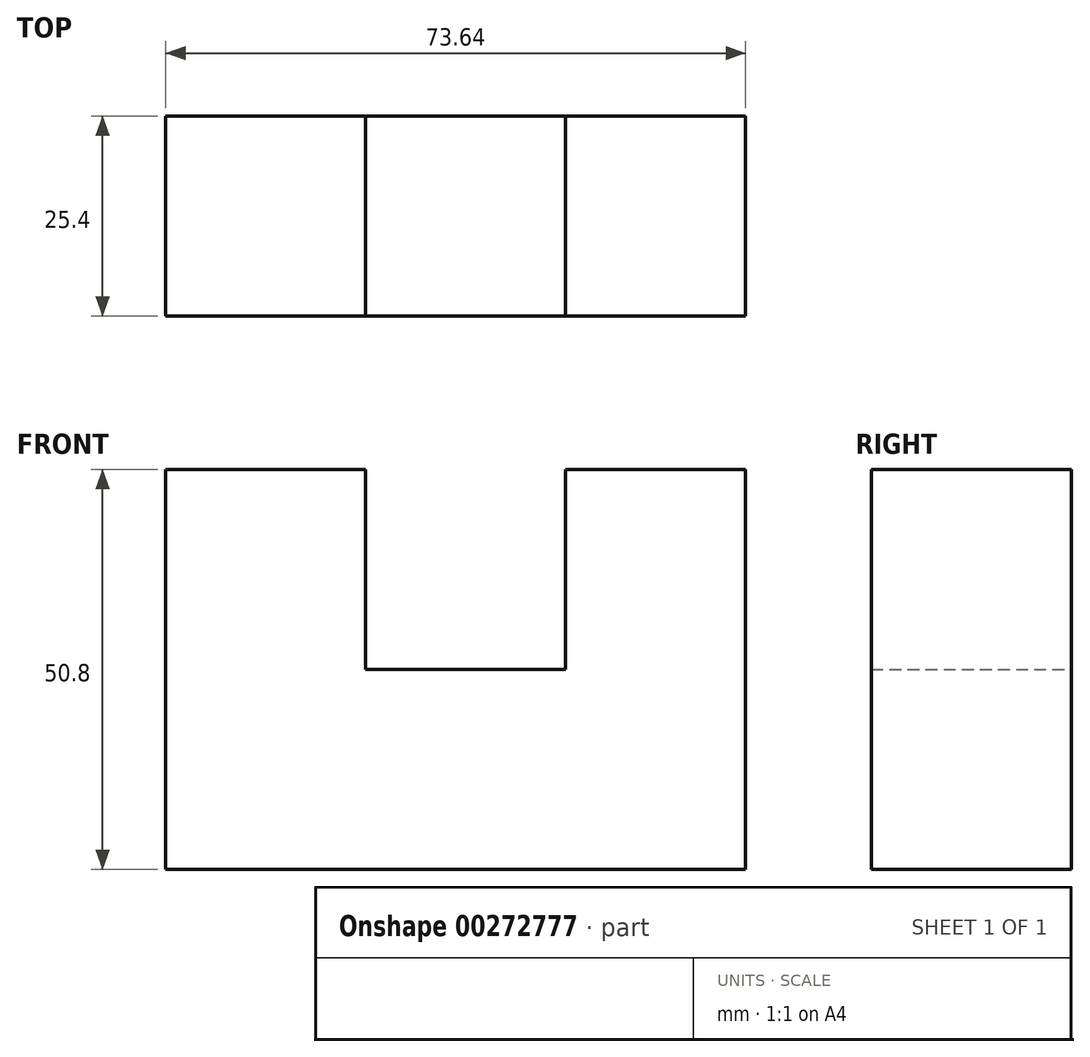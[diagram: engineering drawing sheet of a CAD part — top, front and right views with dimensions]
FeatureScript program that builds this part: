
annotation { "Feature Type Name" : "Feature", "Feature Type Description" : "" }
export const myFeature = defineFeature(function(context is Context, id is Id, definition is map)
    precondition{}
    {
        {
            var Q0;
            Q0=qCreatedBy(makeId("Front.planeOp"),FACE);
            var sketch = newSketch(context, id + "F0", { "sketchPlane" : qUnion([Q0])});
            skLineSegment(sketch, "E0", {"start": v(-73.64, 0) * mm, "end": v(2.56, 0) * mm});
            skLineSegment(sketch, "E1", {"start": v(-73.64, 0) * mm, "end": v(-73.64, 50.8) * mm});
            skLineSegment(sketch, "E2", {"start": v(-73.64, 50.8) * mm, "end": v(-48.24, 50.8) * mm});
            skLineSegment(sketch, "E3", {"start": v(-48.24, 50.8) * mm, "end": v(-48.24, 25.4) * mm});
            skLineSegment(sketch, "E4", {"start": v(-48.24, 25.4) * mm, "end": v(-22.84, 25.4) * mm});
            skLineSegment(sketch, "E5", {"start": v(-22.84, 25.4) * mm, "end": v(-22.84, 50.8) * mm});
            skLineSegment(sketch, "E6", {"start": v(-22.84, 50.8) * mm, "end": v(0, 50.8) * mm});
            skLineSegment(sketch, "E7", {"start": v(0, 50.8) * mm, "end": v(0, 0) * mm});
            skSolve(sketch);
        }
        {
            var Q0;
            Q0 = qSketchRegion(id + "F0", true);
            extrude(context, id + "F1", {"entities" : qUnion([Q0]), "depth" : 25.4 * mm});
        }
    });
